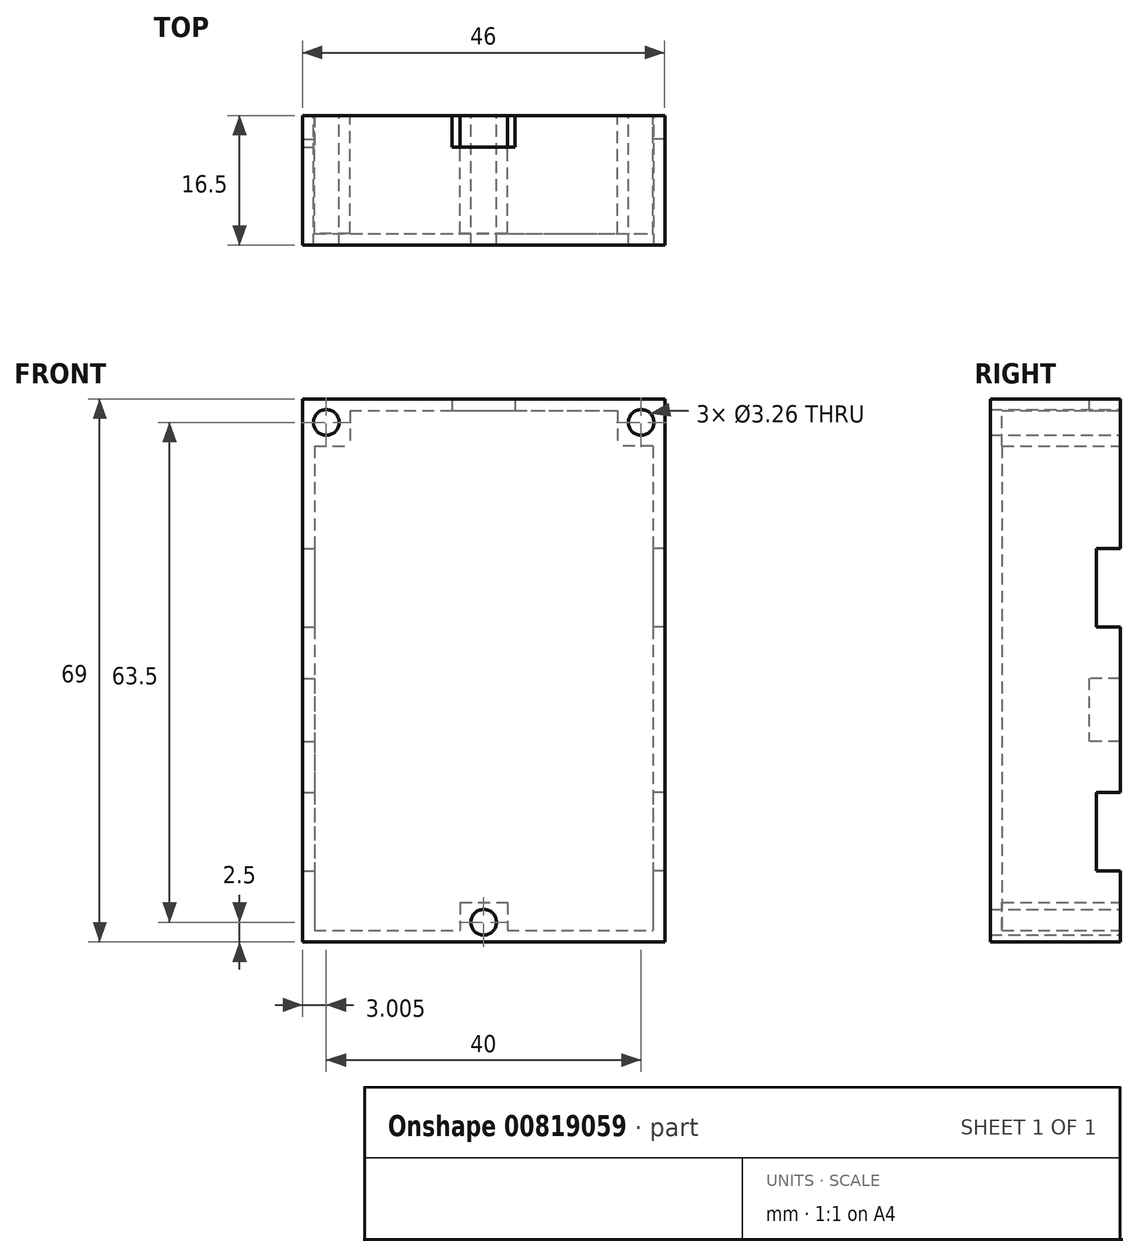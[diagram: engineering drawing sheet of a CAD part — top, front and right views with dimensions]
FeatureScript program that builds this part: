
annotation { "Feature Type Name" : "Feature", "Feature Type Description" : "" }
export const myFeature = defineFeature(function(context is Context, id is Id, definition is map)
    precondition{}
    {
        {
            var Q0;
            Q0=qCreatedBy(makeId("Front.planeOp"),FACE);
            var sketch = newSketch(context, id + "F0", { "sketchPlane" : qUnion([Q0])});
            skCircle(sketch, "E0", {"center": v(-20.38, 33.5) * mm, "radius": 1.14 * mm});
            skCircle(sketch, "E1", {"center": v(-25.88, 18.5) * mm, "radius": 0.89 * mm});
            skCircle(sketch, "E2", {"center": v(-8.88, 18.5) * mm, "radius": 0.89 * mm});
            skCircle(sketch, "E3", {"center": v(-8.88, 6.5) * mm, "radius": 0.89 * mm});
            skCircle(sketch, "E4", {"center": v(-25.88, 6.5) * mm, "radius": 0.89 * mm});
            skCircle(sketch, "E5", {"center": v(-25.87, -12.5) * mm, "radius": 0.89 * mm});
            skCircle(sketch, "E6", {"center": v(-8.88, -12.5) * mm, "radius": 0.89 * mm});
            skCircle(sketch, "E7", {"center": v(-8.88, -24.5) * mm, "radius": 0.89 * mm});
            skCircle(sketch, "E8", {"center": v(-25.87, -24.5) * mm, "radius": 0.89 * mm});
            skCircle(sketch, "E9", {"center": v(-25.38, -29.5) * mm, "radius": 1.14 * mm});
            skCircle(sketch, "E10", {"center": v(-0.38, -30) * mm, "radius": 1.14 * mm});
            skCircle(sketch, "E11", {"center": v(-0.38, -3) * mm, "radius": 2.9 * mm});
            skLineSegment(sketch, "E12", {"start": v(27.62, 36.5) * mm, "end": v(-28.38, 36.5) * mm});
            skLineSegment(sketch, "E13", {"start": v(-28.37, 36.5) * mm, "end": v(-28.38, -32.5) * mm});
            skLineSegment(sketch, "E14", {"start": v(27.63, -32.5) * mm, "end": v(-28.38, -32.5) * mm});
            skLineSegment(sketch, "E15.bottom", {"start": v(-28.38, -32.5) * mm, "end": v(-22.38, -32.5) * mm, "construction": true});
            skLineSegment(sketch, "E15.top", {"start": v(-28.38, -26.5) * mm, "end": v(-22.38, -26.5) * mm, "construction": true});
            skLineSegment(sketch, "E15.left", {"start": v(-28.38, -32.5) * mm, "end": v(-28.38, -26.5) * mm, "construction": true});
            skLineSegment(sketch, "E15.right", {"start": v(-22.38, -32.5) * mm, "end": v(-22.38, -26.5) * mm, "construction": true});
            skLineSegment(sketch, "E16", {"start": v(-28.38, -26.5) * mm, "end": v(-22.38, -32.5) * mm});
            skLineSegment(sketch, "E17", {"start": v(-28.38, -32.5) * mm, "end": v(-22.38, -26.5) * mm});
            skPoint(sketch, "E18", {"position": v(-28.38, 2) * mm});
            skLineSegment(sketch, "E19", {"start": v(-0.38, 36.5) * mm, "end": v(-20.38, 36.5) * mm, "construction": true});
            skLineSegment(sketch, "E20", {"start": v(-20.38, 36.5) * mm, "end": v(-20.38, 33.5) * mm});
            skLineSegment(sketch, "E21", {"start": v(-0.37, -32.5) * mm, "end": v(-0.38, -30) * mm});
            skLineSegment(sketch, "E22", {"start": v(-8.88, -12.5) * mm, "end": v(-8.88, -24.5) * mm, "construction": true});
            skPoint(sketch, "E23", {"position": v(-8.88, -18.5) * mm});
            skLineSegment(sketch, "E24", {"start": v(-8.88, -18.5) * mm, "end": v(-28.37, -18.5) * mm, "construction": true});
            skLineSegment(sketch, "E25", {"start": v(-25.88, -24.5) * mm, "end": v(-25.88, -12.5) * mm, "construction": true});
            skPoint(sketch, "E26", {"position": v(-25.88, -18.5) * mm});
            skPoint(sketch, "E27", {"position": v(-20.88, -18.5) * mm});
            skLineSegment(sketch, "E28", {"start": v(-20.88, -18.5) * mm, "end": v(-20.88, -8.5) * mm, "construction": true});
            skLineSegment(sketch, "E29", {"start": v(-20.88, -8.5) * mm, "end": v(-12.88, -8.5) * mm, "construction": true});
            skLineSegment(sketch, "E30", {"start": v(-12.88, -8.5) * mm, "end": v(-12.88, -28.5) * mm, "construction": true});
            skLineSegment(sketch, "E31.bottom", {"start": v(-20.88, -8.5) * mm, "end": v(-12.88, -8.5) * mm});
            skLineSegment(sketch, "E31.top", {"start": v(-20.88, -28.5) * mm, "end": v(-12.88, -28.5) * mm});
            skLineSegment(sketch, "E31.left", {"start": v(-20.88, -8.5) * mm, "end": v(-20.88, -28.5) * mm});
            skLineSegment(sketch, "E31.right", {"start": v(-12.88, -8.5) * mm, "end": v(-12.88, -28.5) * mm});
            skLineSegment(sketch, "E32", {"start": v(-25.88, 18.5) * mm, "end": v(-25.88, 6.5) * mm, "construction": true});
            skPoint(sketch, "E33", {"position": v(-25.88, 12.5) * mm});
            skLineSegment(sketch, "E34", {"start": v(-8.88, 18.5) * mm, "end": v(-8.88, 6.5) * mm, "construction": true});
            skPoint(sketch, "E35", {"position": v(-8.88, 12.5) * mm});
            skLineSegment(sketch, "E36", {"start": v(-8.88, 12.5) * mm, "end": v(-28.38, 12.5) * mm, "construction": true});
            skLineSegment(sketch, "E37", {"start": v(-25.88, 18.5) * mm, "end": v(-28.38, 18.5) * mm, "construction": true});
            skLineSegment(sketch, "E38", {"start": v(-25.87, -12.5) * mm, "end": v(-28.37, -12.5) * mm, "construction": true});
            skLineSegment(sketch, "E39", {"start": v(-20.88, -8.5) * mm, "end": v(-28.37, -8.5) * mm, "construction": true});
            skLineSegment(sketch, "E40", {"start": v(-28.38, 22.5) * mm, "end": v(-20.88, 22.5) * mm, "construction": true});
            skLineSegment(sketch, "E41", {"start": v(-20.88, 22.5) * mm, "end": v(-20.88, 12.5) * mm});
            skLineSegment(sketch, "E42", {"start": v(-20.88, 22.5) * mm, "end": v(-12.88, 22.5) * mm});
            skLineSegment(sketch, "E43", {"start": v(-12.88, 22.5) * mm, "end": v(-12.87, 2.5) * mm, "construction": true});
            skLineSegment(sketch, "E44.bottom", {"start": v(-20.88, 22.5) * mm, "end": v(-12.88, 22.5) * mm, "construction": true});
            skLineSegment(sketch, "E44.top", {"start": v(-20.88, 2.5) * mm, "end": v(-12.88, 2.5) * mm});
            skLineSegment(sketch, "E44.left", {"start": v(-20.88, 22.5) * mm, "end": v(-20.88, 2.5) * mm});
            skLineSegment(sketch, "E44.right", {"start": v(-12.87, 22.5) * mm, "end": v(-12.87, 2.5) * mm});
            skLineSegment(sketch, "E45", {"start": v(27.62, 36.5) * mm, "end": v(27.63, -32.5) * mm});
            skLineSegment(sketch, "E46", {"start": v(-0.38, -3) * mm, "end": v(-0.37, -30) * mm});
            skLineSegment(sketch, "E47", {"start": v(-0.38, 36.5) * mm, "end": v(-0.38, -3) * mm, "construction": true});
            skLineSegment(sketch, "E48.bottom", {"start": v(-28.38, 36.5) * mm, "end": v(-22.38, 36.5) * mm, "construction": true});
            skLineSegment(sketch, "E48.top", {"start": v(-28.38, 30.5) * mm, "end": v(-22.38, 30.5) * mm, "construction": true});
            skLineSegment(sketch, "E48.left", {"start": v(-28.38, 36.5) * mm, "end": v(-28.38, 30.5) * mm, "construction": true});
            skLineSegment(sketch, "E48.right", {"start": v(-22.38, 36.5) * mm, "end": v(-22.38, 30.5) * mm, "construction": true});
            skLineSegment(sketch, "E49", {"start": v(-28.38, 36.5) * mm, "end": v(-22.38, 30.5) * mm, "construction": true});
            skLineSegment(sketch, "E50", {"start": v(-28.38, 30.5) * mm, "end": v(-22.38, 36.5) * mm, "construction": true});
            skCircle(sketch, "E51", {"center": v(-25.38, 33.5) * mm, "radius": 1.14 * mm});
            skCircle(sketch, "E52.MirrorC", {"center": v(24.62, -29.5) * mm, "radius": 1.14 * mm});
            skCircle(sketch, "E53.MirrorC", {"center": v(25.12, -24.5) * mm, "radius": 0.89 * mm});
            skLineSegment(sketch, "E54.MirrorCS", {"start": v(12.12, -8.5) * mm, "end": v(12.13, -28.5) * mm});
            skLineSegment(sketch, "E55.MirrorCS", {"start": v(20.12, -8.5) * mm, "end": v(12.12, -8.5) * mm});
            skLineSegment(sketch, "E56.MirrorCS", {"start": v(20.12, -8.5) * mm, "end": v(20.12, -28.5) * mm});
            skPoint(sketch, "E57.MirrorP", {"position": v(20.12, -18.5) * mm});
            skLineSegment(sketch, "E58.MirrorCS", {"start": v(20.12, -8.5) * mm, "end": v(12.12, -8.5) * mm, "construction": true});
            skLineSegment(sketch, "E59.MirrorCS", {"start": v(8.12, -12.5) * mm, "end": v(8.13, -24.5) * mm, "construction": true});
            skLineSegment(sketch, "E60.MirrorCS", {"start": v(20.12, -28.5) * mm, "end": v(12.12, -28.5) * mm});
            skLineSegment(sketch, "E61.MirrorCS", {"start": v(20.12, -18.5) * mm, "end": v(20.12, -8.5) * mm, "construction": true});
            skCircle(sketch, "E62.MirrorC", {"center": v(8.13, -24.5) * mm, "radius": 0.89 * mm});
            skCircle(sketch, "E63.MirrorC", {"center": v(8.13, -12.5) * mm, "radius": 0.89 * mm});
            skPoint(sketch, "E64.MirrorP", {"position": v(25.12, -18.5) * mm});
            skPoint(sketch, "E65.MirrorP", {"position": v(8.12, -18.5) * mm});
            skCircle(sketch, "E66.MirrorC", {"center": v(25.12, -12.5) * mm, "radius": 0.89 * mm});
            skLineSegment(sketch, "E67.MirrorCS", {"start": v(25.12, -24.5) * mm, "end": v(25.13, -12.5) * mm, "construction": true});
            skLineSegment(sketch, "E68.MirrorCS", {"start": v(12.12, -8.5) * mm, "end": v(12.13, -28.5) * mm, "construction": true});
            skPoint(sketch, "E69.MirrorP", {"position": v(27.62, 2) * mm});
            skLineSegment(sketch, "E70.MirrorCS", {"start": v(12.12, 22.5) * mm, "end": v(12.12, 2.5) * mm});
            skLineSegment(sketch, "E71.MirrorCS", {"start": v(20.13, 22.5) * mm, "end": v(12.13, 22.5) * mm});
            skCircle(sketch, "E72.MirrorC", {"center": v(25.13, 18.5) * mm, "radius": 0.89 * mm});
            skLineSegment(sketch, "E73.MirrorCS", {"start": v(20.13, 22.5) * mm, "end": v(12.13, 22.5) * mm, "construction": true});
            skLineSegment(sketch, "E74.MirrorCS", {"start": v(20.13, 2.5) * mm, "end": v(12.13, 2.5) * mm});
            skPoint(sketch, "E75.MirrorP", {"position": v(25.13, 12.5) * mm});
            skLineSegment(sketch, "E76.MirrorCS", {"start": v(20.12, 22.5) * mm, "end": v(20.12, 2.5) * mm});
            skCircle(sketch, "E77.MirrorC", {"center": v(8.13, 18.5) * mm, "radius": 0.89 * mm});
            skLineSegment(sketch, "E78.MirrorCS", {"start": v(8.13, 18.5) * mm, "end": v(8.13, 6.5) * mm, "construction": true});
            skLineSegment(sketch, "E79.MirrorCS", {"start": v(12.12, 22.5) * mm, "end": v(12.12, 2.5) * mm, "construction": true});
            skLineSegment(sketch, "E80.MirrorCS", {"start": v(25.13, 18.5) * mm, "end": v(25.13, 6.5) * mm, "construction": true});
            skLineSegment(sketch, "E81.MirrorCS", {"start": v(20.13, 22.5) * mm, "end": v(20.13, 12.5) * mm});
            skCircle(sketch, "E82.MirrorC", {"center": v(25.13, 6.5) * mm, "radius": 0.89 * mm});
            skCircle(sketch, "E83.MirrorC", {"center": v(8.13, 6.5) * mm, "radius": 0.89 * mm});
            skPoint(sketch, "E84.MirrorP", {"position": v(8.13, 12.5) * mm});
            skCircle(sketch, "E85.MirrorC", {"center": v(24.63, 33.5) * mm, "radius": 1.14 * mm});
            skCircle(sketch, "E86.MirrorC", {"center": v(19.63, 33.5) * mm, "radius": 1.14 * mm});
            skSolve(sketch);
        }
        {
            var Q0;
            Q0=qCreatedBy(makeId("Front.planeOp"),FACE);
            var sketch = newSketch(context, id + "F1", { "sketchPlane" : qUnion([Q0])});
            skLineSegment(sketch, "E87.0", {"start": v(-28.37, 36.5) * mm, "end": v(-28.38, -32.5) * mm, "construction": true});
            skLineSegment(sketch, "E87.1", {"start": v(27.62, 36.5) * mm, "end": v(27.63, -32.5) * mm, "construction": true});
            skCircle(sketch, "E88.0", {"center": v(-25.88, 18.5) * mm, "radius": 0.89 * mm, "construction": true});
            skLineSegment(sketch, "E89", {"start": v(-25.88, 18.5) * mm, "end": v(-23.38, 18.5) * mm, "construction": true});
            skLineSegment(sketch, "E90.0", {"start": v(27.62, 36.5) * mm, "end": v(-28.38, 36.5) * mm, "construction": true});
            skLineSegment(sketch, "E90.1", {"start": v(27.63, -32.5) * mm, "end": v(-28.38, -32.5) * mm, "construction": true});
            skLineSegment(sketch, "E91", {"start": v(-23.38, 18.5) * mm, "end": v(-23.38, 36.5) * mm, "construction": true});
            skCircle(sketch, "E92.0", {"center": v(25.12, -24.5) * mm, "radius": 0.89 * mm, "construction": true});
            skLineSegment(sketch, "E93", {"start": v(25.12, -24.5) * mm, "end": v(22.62, -24.5) * mm});
            skLineSegment(sketch, "E94", {"start": v(22.62, -24.5) * mm, "end": v(22.62, -32.5) * mm});
            skLineSegment(sketch, "E95.bottom", {"start": v(-23.38, 36.5) * mm, "end": v(22.62, 36.5) * mm});
            skLineSegment(sketch, "E95.top", {"start": v(-23.38, -32.5) * mm, "end": v(22.62, -32.5) * mm});
            skLineSegment(sketch, "E95.left", {"start": v(-23.38, 36.5) * mm, "end": v(-23.38, -32.5) * mm});
            skLineSegment(sketch, "E95.right", {"start": v(22.62, 36.5) * mm, "end": v(22.62, -32.5) * mm});
            skSolve(sketch);
        }
        {
            var Q0;
            Q0=qCreatedBy(makeId("Front.planeOp"),FACE);
            var sketch = newSketch(context, id + "F2", { "sketchPlane" : qUnion([Q0])});
            skLineSegment(sketch, "E96.0", {"start": v(-23.38, 36.5) * mm, "end": v(-23.38, -32.5) * mm, "construction": true});
            skLineSegment(sketch, "E96.1", {"start": v(-23.38, 36.5) * mm, "end": v(22.62, 36.5) * mm, "construction": true});
            skLineSegment(sketch, "E96.2", {"start": v(22.62, 36.5) * mm, "end": v(22.62, -32.5) * mm, "construction": true});
            skLineSegment(sketch, "E96.3", {"start": v(-23.38, -32.5) * mm, "end": v(22.62, -32.5) * mm, "construction": true});
            skLineSegment(sketch, "E97.0", {"start": v(-21.88, 35) * mm, "end": v(-21.88, -31) * mm});
            skLineSegment(sketch, "E97.1", {"start": v(-21.88, 35) * mm, "end": v(21.12, 35) * mm});
            skLineSegment(sketch, "E97.2", {"start": v(21.12, 35) * mm, "end": v(21.12, -31) * mm});
            skLineSegment(sketch, "E97.3", {"start": v(-21.88, -31) * mm, "end": v(21.12, -31) * mm});
            skSolve(sketch);
        }
        {
            var Q0;
            Q0=qCreatedBy(makeId("Front.planeOp"),FACE);
            var sketch = newSketch(context, id + "F3", { "sketchPlane" : qUnion([Q0])});
            skLineSegment(sketch, "E98.0", {"start": v(-23.38, 36.5) * mm, "end": v(22.62, 36.5) * mm, "construction": true});
            skLineSegment(sketch, "E98.1", {"start": v(-23.38, 36.5) * mm, "end": v(-23.38, -32.5) * mm, "construction": true});
            skLineSegment(sketch, "E98.2", {"start": v(22.62, 36.5) * mm, "end": v(22.62, -32.5) * mm, "construction": true});
            skLineSegment(sketch, "E98.3", {"start": v(-23.38, -32.5) * mm, "end": v(22.62, -32.5) * mm, "construction": true});
            skLineSegment(sketch, "E99.bottom", {"start": v(-23.38, 36.5) * mm, "end": v(-17.38, 36.5) * mm});
            skLineSegment(sketch, "E99.top", {"start": v(-23.38, 30.5) * mm, "end": v(-17.38, 30.5) * mm});
            skLineSegment(sketch, "E99.left", {"start": v(-23.38, 36.5) * mm, "end": v(-23.38, 30.5) * mm});
            skLineSegment(sketch, "E99.right", {"start": v(-17.38, 36.5) * mm, "end": v(-17.38, 30.5) * mm});
            skLineSegment(sketch, "E100", {"start": v(-23.38, 36.5) * mm, "end": v(-17.38, 30.5) * mm, "construction": true});
            skLineSegment(sketch, "E101", {"start": v(-23.38, 30.5) * mm, "end": v(-17.38, 36.5) * mm, "construction": true});
            skPoint(sketch, "E102", {"position": v(-20.38, 33.5) * mm});
            skCircle(sketch, "E103", {"center": v(-20.38, 33.5) * mm, "radius": 1.63 * mm});
            skPoint(sketch, "E104", {"position": v(-0.38, 36.5) * mm});
            skLineSegment(sketch, "E105", {"start": v(-0.38, 36.5) * mm, "end": v(-0.38, -32.5) * mm, "construction": true});
            skLineSegment(sketch, "E106.MirrorCS", {"start": v(22.62, 36.5) * mm, "end": v(22.62, 30.5) * mm});
            skLineSegment(sketch, "E107.MirrorCS", {"start": v(22.62, 36.5) * mm, "end": v(16.62, 36.5) * mm});
            skLineSegment(sketch, "E108.MirrorCS", {"start": v(22.62, 30.5) * mm, "end": v(16.62, 30.5) * mm});
            skLineSegment(sketch, "E109.MirrorCS", {"start": v(16.62, 36.5) * mm, "end": v(16.62, 30.5) * mm});
            skCircle(sketch, "E110.MirrorC", {"center": v(19.62, 33.5) * mm, "radius": 1.63 * mm});
            skLineSegment(sketch, "E111.bottom", {"start": v(-3.38, -27.5) * mm, "end": v(2.62, -27.5) * mm});
            skLineSegment(sketch, "E111.top", {"start": v(-3.38, -32.5) * mm, "end": v(2.62, -32.5) * mm});
            skLineSegment(sketch, "E111.left", {"start": v(-3.38, -27.5) * mm, "end": v(-3.38, -32.5) * mm});
            skLineSegment(sketch, "E111.right", {"start": v(2.62, -27.5) * mm, "end": v(2.62, -32.5) * mm});
            skPoint(sketch, "E112", {"position": v(-0.38, -32.5) * mm});
            skLineSegment(sketch, "E113", {"start": v(-3.38, -27.5) * mm, "end": v(2.62, -32.5) * mm, "construction": true});
            skLineSegment(sketch, "E114", {"start": v(-3.38, -32.5) * mm, "end": v(2.62, -27.5) * mm, "construction": true});
            skCircle(sketch, "E115", {"center": v(-0.38, -30) * mm, "radius": 1.63 * mm});
            skLineSegment(sketch, "E116.0", {"start": v(-25.88, -24.5) * mm, "end": v(-25.88, -12.5) * mm, "construction": true});
            skPoint(sketch, "E117", {"position": v(-25.88, -18.5) * mm});
            skLineSegment(sketch, "E118.bottom", {"start": v(-25.88, -13.5) * mm, "end": v(-19.88, -13.5) * mm});
            skLineSegment(sketch, "E118.top", {"start": v(-25.88, -23.5) * mm, "end": v(-19.88, -23.5) * mm});
            skLineSegment(sketch, "E118.left", {"start": v(-25.88, -13.5) * mm, "end": v(-25.88, -23.5) * mm});
            skLineSegment(sketch, "E118.right", {"start": v(-19.88, -13.5) * mm, "end": v(-19.88, -23.5) * mm});
            skLineSegment(sketch, "E119.bottom", {"start": v(-25.88, 17.5) * mm, "end": v(-19.87, 17.5) * mm});
            skLineSegment(sketch, "E119.top", {"start": v(-25.88, 7.5) * mm, "end": v(-19.87, 7.5) * mm});
            skLineSegment(sketch, "E119.left", {"start": v(-25.88, 17.5) * mm, "end": v(-25.88, 7.5) * mm});
            skLineSegment(sketch, "E119.right", {"start": v(-19.88, 17.5) * mm, "end": v(-19.88, 7.5) * mm});
            skPoint(sketch, "E120", {"position": v(-25.88, 12.5) * mm});
            skLineSegment(sketch, "E121.bottom", {"start": v(-25.88, 1) * mm, "end": v(-19.88, 1) * mm});
            skLineSegment(sketch, "E121.top", {"start": v(-25.88, -7) * mm, "end": v(-19.88, -7) * mm});
            skLineSegment(sketch, "E121.left", {"start": v(-25.88, 1) * mm, "end": v(-25.88, -7) * mm});
            skLineSegment(sketch, "E121.right", {"start": v(-19.88, 1) * mm, "end": v(-19.88, -7) * mm});
            skPoint(sketch, "E122", {"position": v(-25.88, -3) * mm});
            skCircle(sketch, "E123.0", {"center": v(-25.88, 6.5) * mm, "radius": 0.89 * mm});
            skLineSegment(sketch, "E123.1", {"start": v(-25.88, 18.5) * mm, "end": v(-25.88, 6.5) * mm});
            skLineSegment(sketch, "E124", {"start": v(-25.88, 6.5) * mm, "end": v(-25.88, -12.5) * mm, "construction": true});
            skLineSegment(sketch, "E125.bottom", {"start": v(-4.38, 36.5) * mm, "end": v(3.62, 36.5) * mm});
            skLineSegment(sketch, "E125.top", {"start": v(-4.38, 30.5) * mm, "end": v(3.62, 30.5) * mm});
            skLineSegment(sketch, "E125.left", {"start": v(-4.38, 36.5) * mm, "end": v(-4.38, 30.5) * mm});
            skLineSegment(sketch, "E125.right", {"start": v(3.62, 36.5) * mm, "end": v(3.62, 30.5) * mm});
            skLineSegment(sketch, "E126.MirrorCS", {"start": v(25.12, -13.5) * mm, "end": v(25.12, -23.5) * mm});
            skLineSegment(sketch, "E127.MirrorCS", {"start": v(25.12, -23.5) * mm, "end": v(19.12, -23.5) * mm});
            skLineSegment(sketch, "E128.MirrorCS", {"start": v(19.12, -13.5) * mm, "end": v(19.12, -23.5) * mm});
            skLineSegment(sketch, "E129.MirrorCS", {"start": v(25.12, -13.5) * mm, "end": v(19.12, -13.5) * mm});
            skLineSegment(sketch, "E130.MirrorCS", {"start": v(25.12, 17.5) * mm, "end": v(19.12, 17.5) * mm});
            skLineSegment(sketch, "E131.MirrorCS", {"start": v(19.12, 17.5) * mm, "end": v(19.12, 7.5) * mm});
            skLineSegment(sketch, "E132.MirrorCS", {"start": v(25.12, 17.5) * mm, "end": v(25.12, 7.5) * mm});
            skLineSegment(sketch, "E133.MirrorCS", {"start": v(25.12, 7.5) * mm, "end": v(19.12, 7.5) * mm});
            skSolve(sketch);
        }
        {
            var Q0;
            Q0=qCreatedBy(makeId("Front.planeOp"),FACE);
            var sketch = newSketch(context, id + "F4", { "sketchPlane" : qUnion([Q0])});
            skLineSegment(sketch, "E134.0", {"start": v(-23.38, 30.5) * mm, "end": v(-17.38, 30.5) * mm});
            skLineSegment(sketch, "E134.1", {"start": v(-17.38, 36.5) * mm, "end": v(-17.38, 30.5) * mm});
            skLineSegment(sketch, "E134.2", {"start": v(16.62, 36.5) * mm, "end": v(16.62, 30.5) * mm});
            skLineSegment(sketch, "E134.3", {"start": v(22.62, 30.5) * mm, "end": v(16.62, 30.5) * mm});
            skLineSegment(sketch, "E134.4", {"start": v(-3.38, -27.5) * mm, "end": v(2.62, -27.5) * mm});
            skLineSegment(sketch, "E134.5", {"start": v(-3.38, -27.5) * mm, "end": v(-3.38, -32.5) * mm});
            skLineSegment(sketch, "E134.6", {"start": v(2.62, -27.5) * mm, "end": v(2.62, -32.5) * mm});
            skLineSegment(sketch, "E134.7", {"start": v(-3.38, -32.5) * mm, "end": v(2.62, -32.5) * mm});
            skLineSegment(sketch, "E134.8", {"start": v(-23.38, 36.5) * mm, "end": v(-17.38, 36.5) * mm});
            skLineSegment(sketch, "E134.9", {"start": v(-23.38, 36.5) * mm, "end": v(-23.38, 30.5) * mm});
            skLineSegment(sketch, "E135.0", {"start": v(22.62, 36.5) * mm, "end": v(16.62, 36.5) * mm});
            skLineSegment(sketch, "E135.1", {"start": v(22.62, 36.5) * mm, "end": v(22.62, 30.5) * mm});
            skLineSegment(sketch, "E135.2", {"start": v(27.62, 36.5) * mm, "end": v(-28.38, 36.5) * mm, "construction": true});
            skSolve(sketch);
        }
        {
            var Q0;
            Q0=qCreatedBy(makeId("Front.planeOp"),FACE);
            var sketch = newSketch(context, id + "F5", { "sketchPlane" : qUnion([Q0])});
            skLineSegment(sketch, "E136.0", {"start": v(-4.38, 30.5) * mm, "end": v(3.62, 30.5) * mm});
            skLineSegment(sketch, "E136.1", {"start": v(-21.88, 35) * mm, "end": v(21.12, 35) * mm, "construction": true});
            skLineSegment(sketch, "E136.2", {"start": v(-4.38, 36.5) * mm, "end": v(-4.38, 30.5) * mm});
            skLineSegment(sketch, "E136.3", {"start": v(-4.38, 36.5) * mm, "end": v(3.62, 36.5) * mm});
            skLineSegment(sketch, "E136.4", {"start": v(3.62, 36.5) * mm, "end": v(3.62, 30.5) * mm});
            skLineSegment(sketch, "E137.0", {"start": v(-25.88, 1) * mm, "end": v(-19.88, 1) * mm});
            skLineSegment(sketch, "E137.1", {"start": v(-25.88, 1) * mm, "end": v(-25.88, -7) * mm});
            skLineSegment(sketch, "E137.2", {"start": v(-25.88, -7) * mm, "end": v(-19.88, -7) * mm});
            skLineSegment(sketch, "E137.3", {"start": v(-19.88, 1) * mm, "end": v(-19.88, -7) * mm});
            skSolve(sketch);
        }
        {
            var Q0;
            Q0=qCreatedBy(makeId("Front.planeOp"),FACE);
            var sketch = newSketch(context, id + "F6", { "sketchPlane" : qUnion([Q0])});
            skLineSegment(sketch, "E138.0", {"start": v(-25.88, 17.5) * mm, "end": v(-19.87, 17.5) * mm});
            skLineSegment(sketch, "E138.1", {"start": v(-19.88, 17.5) * mm, "end": v(-19.88, 7.5) * mm});
            skLineSegment(sketch, "E138.2", {"start": v(-25.88, 7.5) * mm, "end": v(-19.87, 7.5) * mm});
            skLineSegment(sketch, "E138.3", {"start": v(-25.88, 17.5) * mm, "end": v(-25.88, 7.5) * mm});
            skLineSegment(sketch, "E138.4", {"start": v(-25.88, -13.5) * mm, "end": v(-25.88, -23.5) * mm});
            skLineSegment(sketch, "E138.5", {"start": v(-25.88, -13.5) * mm, "end": v(-19.88, -13.5) * mm});
            skLineSegment(sketch, "E138.6", {"start": v(-19.88, -13.5) * mm, "end": v(-19.88, -23.5) * mm});
            skLineSegment(sketch, "E138.7", {"start": v(-25.88, -23.5) * mm, "end": v(-19.88, -23.5) * mm});
            skLineSegment(sketch, "E138.8", {"start": v(25.12, 17.5) * mm, "end": v(19.12, 17.5) * mm});
            skLineSegment(sketch, "E138.9", {"start": v(19.12, 17.5) * mm, "end": v(19.12, 7.5) * mm});
            skLineSegment(sketch, "E138.10", {"start": v(25.12, 7.5) * mm, "end": v(19.12, 7.5) * mm});
            skLineSegment(sketch, "E138.11", {"start": v(25.12, 17.5) * mm, "end": v(25.12, 7.5) * mm});
            skLineSegment(sketch, "E138.12", {"start": v(25.12, -13.5) * mm, "end": v(19.12, -13.5) * mm});
            skLineSegment(sketch, "E138.13", {"start": v(19.12, -13.5) * mm, "end": v(19.12, -23.5) * mm});
            skLineSegment(sketch, "E138.14", {"start": v(25.12, -13.5) * mm, "end": v(25.12, -23.5) * mm});
            skLineSegment(sketch, "E138.15", {"start": v(25.12, -23.5) * mm, "end": v(19.12, -23.5) * mm});
            skSolve(sketch);
        }
        {
            var Q0;
            Q0=qCreatedBy(makeId("Front.planeOp"),FACE);
            var sketch = newSketch(context, id + "F7", { "sketchPlane" : qUnion([Q0])});
            skCircle(sketch, "E139.0", {"center": v(-0.38, -30) * mm, "radius": 1.63 * mm});
            skCircle(sketch, "E139.1", {"center": v(-20.38, 33.5) * mm, "radius": 1.63 * mm});
            skCircle(sketch, "E139.2", {"center": v(19.62, 33.5) * mm, "radius": 1.63 * mm});
            skSolve(sketch);
        }
        {
            var Q0;
            Q0=makeQuery(id+"F1.imprint","IMPRINT",FACE,{"disambiguationData":[TD([[makeQuery(id+"F1.imprint","IMPRINT",EDGE,{"derivedFrom":sQuery(id+"F1.wireOp",EDGE,"E94")}),-1.0]])]});
            extrude(context, id + "F8", {"entities" : qUnion([Q0]), "depth" : 16.5 * mm, "offsetDistance" : 25 * mm});
        }
        {
            var Q0;
            Q0 = qSketchRegion(id + "F2", true);
            extrude(context, id + "F9", {"entities" : qUnion([Q0]), "operationType" : NewBodyOperationType.REMOVE, "depth" : 15 * mm, "offsetDistance" : 25 * mm});
        }
        {
            var Q0;
            Q0 = qSketchRegion(id + "F4", true);
            var Q1;
            Q1=makeQuery(id+"F8.opExtrude","CAP_FACE",FACE,{"disambiguationData":[OSD([sQuery(id+"F1.wireOp",EDGE,"E94"),sQuery(id+"F1.wireOp",EDGE,"E95.bottom"),sQuery(id+"F1.wireOp",EDGE,"E95.top"),sQuery(id+"F1.wireOp",EDGE,"E95.left"),sQuery(id+"F1.wireOp",EDGE,"E95.right")])],"isStart":false});
            extrude(context, id + "F10", {"entities" : qUnion([Q0]), "operationType" : NewBodyOperationType.ADD, "endBound" : BoundingType.UP_TO_SURFACE, "depth" : 25 * mm, "endBoundEntityFace" : qUnion([Q1]), "offsetDistance" : 25 * mm});
        }
        {
            var Q0;
            Q0 = qSketchRegion(id + "F5", true);
            extrude(context, id + "F11", {"entities" : qUnion([Q0]), "operationType" : NewBodyOperationType.REMOVE, "depth" : 4 * mm, "offsetDistance" : 25 * mm});
        }
        {
            var Q0;
            Q0 = qSketchRegion(id + "F6", true);
            extrude(context, id + "F12", {"entities" : qUnion([Q0]), "operationType" : NewBodyOperationType.REMOVE, "depth" : 3 * mm, "offsetDistance" : 25 * mm});
        }
        {
            var Q0;
            Q0 = qSketchRegion(id + "F7", true);
            extrude(context, id + "F13", {"entities" : qUnion([Q0]), "operationType" : NewBodyOperationType.REMOVE, "endBound" : BoundingType.THROUGH_ALL, "depth" : 25 * mm, "offsetDistance" : 25 * mm});
        }
    });
